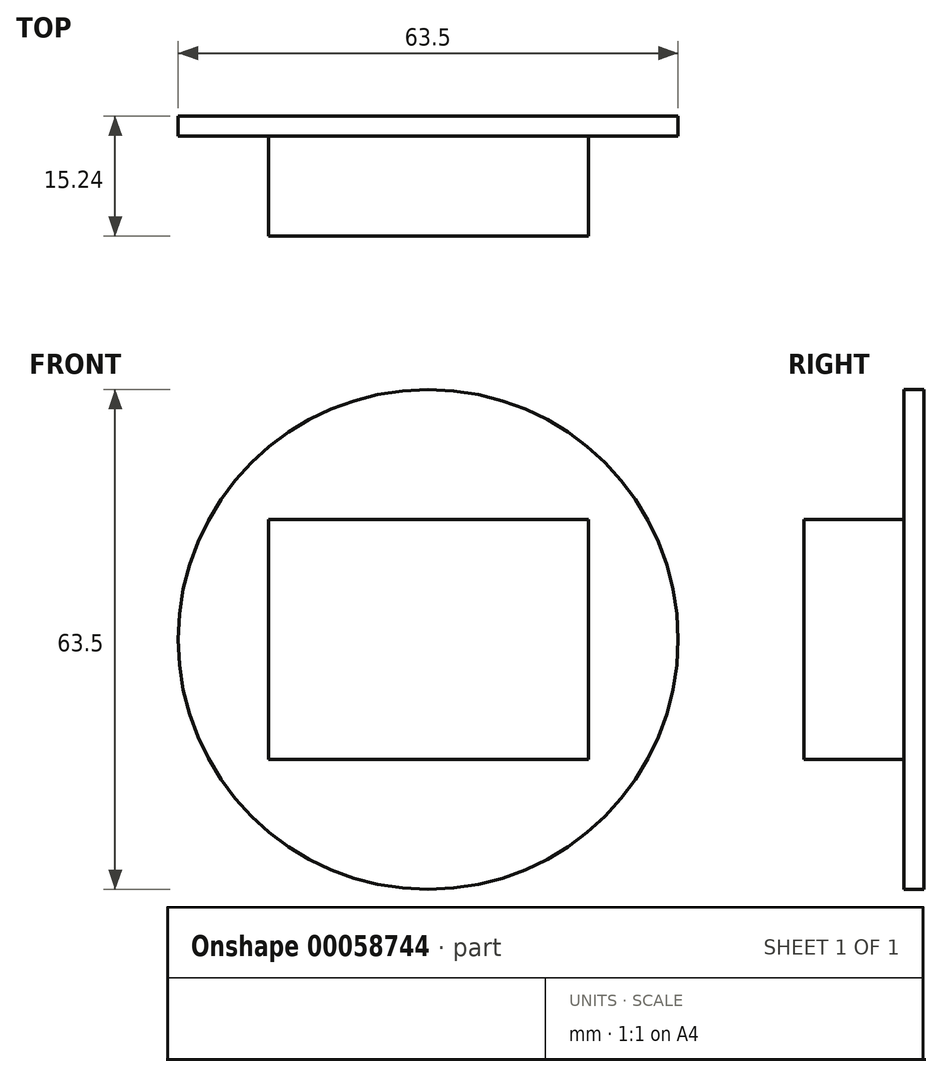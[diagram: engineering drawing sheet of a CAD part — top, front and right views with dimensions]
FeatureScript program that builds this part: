
annotation { "Feature Type Name" : "Feature", "Feature Type Description" : "" }
export const myFeature = defineFeature(function(context is Context, id is Id, definition is map)
    precondition{}
    {
        {
            var Q0;
            Q0=qCreatedBy(makeId("Front.planeOp"),FACE);
            var sketch = newSketch(context, id + "F0", { "sketchPlane" : qUnion([Q0])});
            skCircle(sketch, "E0", {"center": v(0, 0) * mm, "radius": 31.75 * mm});
            skLineSegment(sketch, "E1", {"start": v(-20.25, -15.24) * mm, "end": v(-20.25, 15.24) * mm});
            skLineSegment(sketch, "E2", {"start": v(20.39, -15.24) * mm, "end": v(20.39, 15.24) * mm});
            skLineSegment(sketch, "E3", {"start": v(20.39, 15.24) * mm, "end": v(-20.25, 15.24) * mm});
            skLineSegment(sketch, "E4", {"start": v(-20.25, -15.24) * mm, "end": v(20.39, -15.24) * mm});
            skSolve(sketch);
        }
        {
            var Q0;
            Q0 = qSketchRegion(id + "F0", true);
            extrude(context, id + "F1", {"entities" : qUnion([Q0]), "depth" : 2.54 * mm});
        }
        {
            var Q0;
            Q0=makeQuery(id+"F0.imprint","IMPRINT",FACE,{"disambiguationData":[TD([[makeQuery(id+"F0.imprint","IMPRINT",EDGE,{"derivedFrom":sQuery(id+"F0.wireOp",EDGE,"E1")}),-1.0]])]});
            extrude(context, id + "F2", {"entities" : qUnion([Q0]), "operationType" : NewBodyOperationType.ADD, "depth" : 15.24 * mm});
        }
    });
